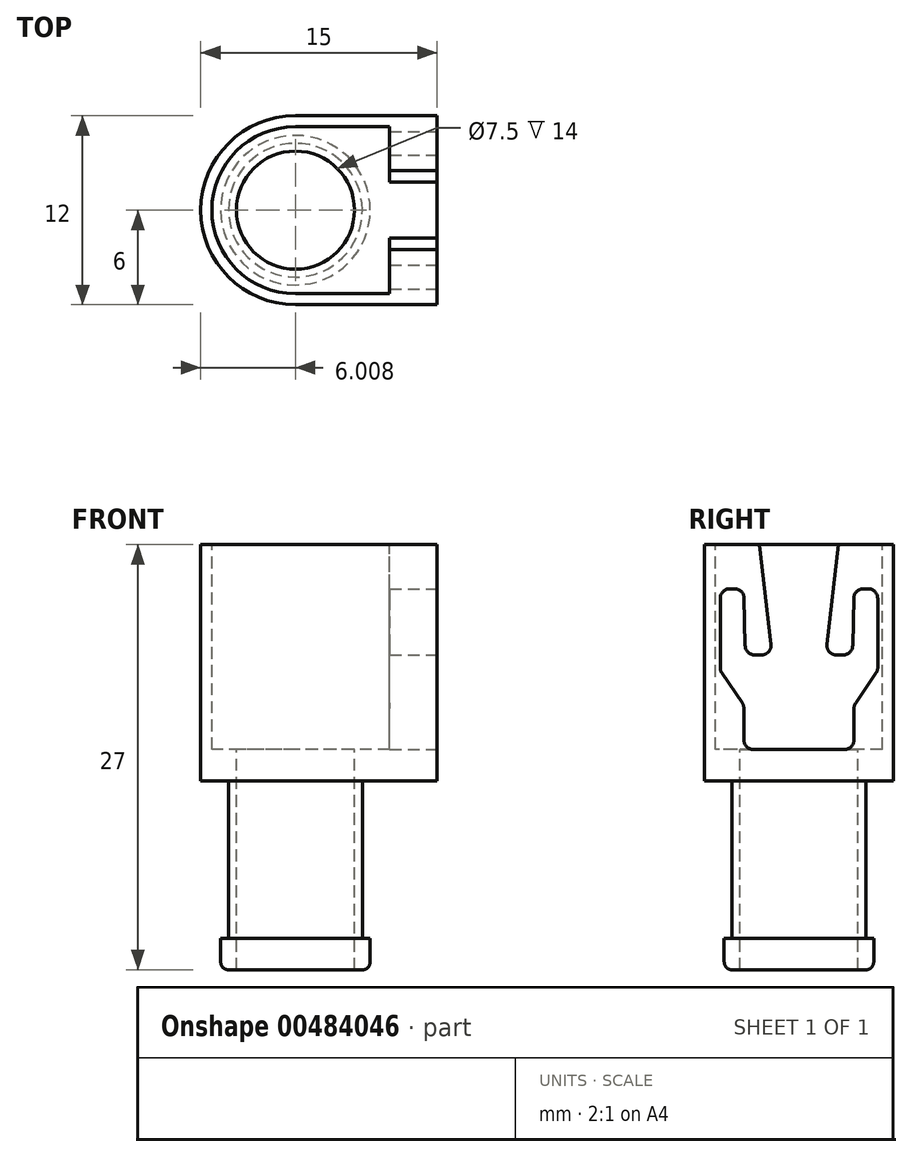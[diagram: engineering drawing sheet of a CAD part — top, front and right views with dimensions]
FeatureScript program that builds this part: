
annotation { "Feature Type Name" : "Feature", "Feature Type Description" : "" }
export const myFeature = defineFeature(function(context is Context, id is Id, definition is map)
    precondition{}
    {
        {
            var Q0;
            Q0=qCreatedBy(makeId("Top.planeOp"),FACE);
            var sketch = newSketch(context, id + "F0", { "sketchPlane" : qUnion([Q0])});
            skLineSegment(sketch, "E0", {"start": v(-9, 6) * mm, "end": v(0, 6) * mm});
            skLineSegment(sketch, "E1", {"start": v(0, 6) * mm, "end": v(0, -6) * mm});
            skLineSegment(sketch, "E2", {"start": v(0, -6) * mm, "end": v(-9, -6) * mm});
            skArc(sketch, "E3", {"start": v(-9, 6) * mm, "mid": v(-15, 0) * mm, "end": v(-9, -6) * mm});
            skSolve(sketch);
        }
        {
            var Q0;
            Q0=makeQuery(id+"F0.imprint","IMPRINT",FACE,{"disambiguationData":[TD([[makeQuery(id+"F0.imprint","IMPRINT",EDGE,{"derivedFrom":sQuery(id+"F0.wireOp",EDGE,"E0")}),-1.0]])]});
            extrude(context, id + "F1", {"entities" : qUnion([Q0]), "depth" : 15 * mm});
        }
        {
            var Q0;
            Q0=qCreatedBy(makeId("Top.planeOp"),FACE);
            var sketch = newSketch(context, id + "F2", { "sketchPlane" : qUnion([Q0])});
            skCircle(sketch, "E4", {"center": v(-9, 0) * mm, "radius": 4.25 * mm});
            skCircle(sketch, "E5", {"center": v(-9, 0) * mm, "radius": 3.75 * mm});
            skSolve(sketch);
        }
        {
            var Q0;
            Q0=makeQuery(id+"F2.imprint","IMPRINT",FACE,{"disambiguationData":[TD([[makeQuery(id+"F2.imprint","IMPRINT",EDGE,{"derivedFrom":sQuery(id+"F2.wireOp",EDGE,"E4")}),1.0]])]});
            extrude(context, id + "F3", {"entities" : qUnion([Q0]), "operationType" : NewBodyOperationType.ADD, "oppositeDirection" : true, "depth" : 10 * mm});
        }
        {
            var Q0;
            Q0=makeQuery(id+"F3.opExtrude","CAP_FACE",FACE,{"disambiguationData":[OSD([sQuery(id+"F2.wireOp",EDGE,"E4"),sQuery(id+"F2.wireOp",EDGE,"E5")])],"isStart":false});
            var sketch = newSketch(context, id + "F4", { "sketchPlane" : qUnion([Q0])});
            skCircle(sketch, "E6", {"center": v(-9, 0) * mm, "radius": 4.75 * mm});
            skSolve(sketch);
        }
        {
            var Q0;
            Q0=makeQuery(id+"F4.imprint","IMPRINT",FACE,{"disambiguationData":[TD([[makeQuery(id+"F4.imprint","IMPRINT",EDGE,{"derivedFrom":makeQuery(id+"F3.opExtrude","CAP_EDGE",EDGE,{"disambiguationData":[OSD([sQuery(id+"F2.wireOp",EDGE,"E4")])],"isStart":false})}),-1.0]])]});
            var Q1;
            Q1=makeQuery(id+"F4.imprint","IMPRINT",FACE,{"disambiguationData":[TD([[makeQuery(id+"F4.imprint","IMPRINT",EDGE,{"derivedFrom":sQuery(id+"F4.wireOp",EDGE,"E6")}),1.0]])]});
            extrude(context, id + "F5", {"entities" : qUnion([Q0, Q1]), "operationType" : NewBodyOperationType.ADD, "depth" : 2 * mm});
        }
        {
            var Q0;
            Q0=makeQuery(id+"F1.opExtrude","CAP_FACE",FACE,{"disambiguationData":[OSD([sQuery(id+"F0.wireOp",EDGE,"E0"),sQuery(id+"F0.wireOp",EDGE,"E1"),sQuery(id+"F0.wireOp",EDGE,"E2"),sQuery(id+"F0.wireOp",EDGE,"E3")])],"isStart":false});
            var sketch = newSketch(context, id + "F6", { "sketchPlane" : qUnion([Q0])});
            skLineSegment(sketch, "E7", {"start": v(-3, 5.3) * mm, "end": v(-9, 5.3) * mm});
            skLineSegment(sketch, "E8", {"start": v(-3, 5.3) * mm, "end": v(-3, -5.3) * mm});
            skLineSegment(sketch, "E9", {"start": v(-3, -5.3) * mm, "end": v(-9, -5.3) * mm});
            skArc(sketch, "E10", {"start": v(-9, 5.3) * mm, "mid": v(-14.3, 0) * mm, "end": v(-9, -5.3) * mm});
            skSolve(sketch);
        }
        {
            var Q0;
            Q0=makeQuery(id+"F6.imprint","IMPRINT",FACE,{"disambiguationData":[TD([[makeQuery(id+"F6.imprint","IMPRINT",EDGE,{"derivedFrom":sQuery(id+"F6.wireOp",EDGE,"E7")}),1.0]])]});
            var Q1;
            {var subQ0=sQuery(id+"F0.wireOp",EDGE,"E2");var subQ1=sQuery(id+"F0.wireOp",EDGE,"E1");var subQ2=sQuery(id+"F0.wireOp",EDGE,"E3");var subQ3=sQuery(id+"F0.wireOp",EDGE,"E0");Q1=makeQuery(id+"F3.boolean.opBoolean","SPLIT",FACE,{"disambiguationData":[TD([makeQuery(id+"F1.opExtrude","SWEPT_FACE",FACE,{"disambiguationData":[OSD([subQ3])]})])],"derivedFrom":makeQuery(id+"F1.opExtrude","CAP_FACE",FACE,{"disambiguationData":[OSD([subQ3,subQ1,subQ0,subQ2])],"isStart":true})});}
            extrude(context, id + "F7", {"entities" : qUnion([Q0]), "operationType" : NewBodyOperationType.REMOVE, "oppositeDirection" : true, "endBoundEntityFace" : qUnion([Q1]), "depth" : 13 * mm, "offsetDistance" : 25.4 * mm});
        }
        {
            var Q0;
            Q0=makeQuery(id+"F3.boolean.opBoolean","SPLIT",FACE,{"disambiguationData":[TD([makeQuery(id+"F3.opExtrude","SWEPT_FACE",FACE,{"disambiguationData":[OSD([sQuery(id+"F2.wireOp",EDGE,"E5")])]})])],"derivedFrom":makeQuery(id+"F1.opExtrude","CAP_FACE",FACE,{"disambiguationData":[OSD([sQuery(id+"F0.wireOp",EDGE,"E0"),sQuery(id+"F0.wireOp",EDGE,"E1"),sQuery(id+"F0.wireOp",EDGE,"E2"),sQuery(id+"F0.wireOp",EDGE,"E3")])],"isStart":true})});
            var Q1;
            Q1=makeQuery(id+"F7.boolean.opBoolean","COPY",FACE,{"derivedFrom":makeQuery(id+"F7.opExtrude","CAP_FACE",FACE,{"disambiguationData":[OSD([sQuery(id+"F6.wireOp",EDGE,"E7"),sQuery(id+"F6.wireOp",EDGE,"E8"),sQuery(id+"F6.wireOp",EDGE,"E9"),sQuery(id+"F6.wireOp",EDGE,"E10")])],"isStart":false})});
            extrude(context, id + "F8", {"entities" : qUnion([Q0]), "operationType" : NewBodyOperationType.REMOVE, "endBound" : BoundingType.UP_TO_SURFACE, "oppositeDirection" : true, "endBoundEntityFace" : qUnion([Q1]), "depth" : 25.4 * mm, "offsetDistance" : 25.4 * mm});
        }
        {
            var Q0;
            Q0=makeQuery(id+"F1.opExtrude","SWEPT_FACE",FACE,{"disambiguationData":[OSD([sQuery(id+"F0.wireOp",EDGE,"E1")])]});
            var sketch = newSketch(context, id + "F9", { "sketchPlane" : qUnion([Q0])});
            skLineSegment(sketch, "E11", {"start": v(-3.5, 2.6) * mm, "end": v(-3.5, 4.61) * mm});
            skLineSegment(sketch, "E12", {"start": v(-3.6, 4.95) * mm, "end": v(-4.9, 6.85) * mm});
            skLineSegment(sketch, "E13", {"start": v(-5, 7.19) * mm, "end": v(-5, 11.6) * mm});
            skLineSegment(sketch, "E14", {"start": v(-4.4, 12.2) * mm, "end": v(-4.1, 12.2) * mm});
            skLineSegment(sketch, "E15", {"start": v(-3.49, 11.6) * mm, "end": v(-3.41, 8.6) * mm});
            skLineSegment(sketch, "E16", {"start": v(-2.8, 8) * mm, "end": v(-2.38, 8) * mm});
            skLineSegment(sketch, "E17", {"start": v(-1.78, 8.67) * mm, "end": v(-2.5, 14.97) * mm});
            skLineSegment(sketch, "E18", {"start": v(-2.9, 2) * mm, "end": v(0, 2) * mm});
            skLineSegment(sketch, "E19.MirrorCS", {"start": v(1.78, 8.67) * mm, "end": v(2.5, 14.97) * mm});
            skLineSegment(sketch, "E20.MirrorCS", {"start": v(2.8, 8) * mm, "end": v(2.38, 8) * mm});
            skLineSegment(sketch, "E21.MirrorCS", {"start": v(3.49, 11.6) * mm, "end": v(3.41, 8.6) * mm});
            skLineSegment(sketch, "E22.MirrorCS", {"start": v(4.4, 12.2) * mm, "end": v(4.1, 12.2) * mm});
            skLineSegment(sketch, "E23.MirrorCS", {"start": v(5, 7.19) * mm, "end": v(5, 11.6) * mm});
            skLineSegment(sketch, "E24.MirrorCS", {"start": v(3.6, 4.95) * mm, "end": v(4.9, 6.85) * mm});
            skLineSegment(sketch, "E25.MirrorCS", {"start": v(2.9, 2) * mm, "end": v(0, 2) * mm});
            skLineSegment(sketch, "E26.MirrorCS", {"start": v(3.5, 2.6) * mm, "end": v(3.5, 4.61) * mm});
            skPoint(sketch, "E27.visualSharp", {"position": v(3.4, 8) * mm});
            skArc(sketch, "E27.filletArc", {"start": v(2.8, 8) * mm, "mid": v(3.23, 8.17) * mm, "end": v(3.41, 8.6) * mm});
            skPoint(sketch, "E28.visualSharp", {"position": v(1.7, 8) * mm});
            skArc(sketch, "E28.filletArc", {"start": v(1.78, 8.67) * mm, "mid": v(1.93, 8.2) * mm, "end": v(2.38, 8) * mm});
            skPoint(sketch, "E29.visualSharp", {"position": v(-1.7, 8) * mm});
            skArc(sketch, "E29.filletArc", {"start": v(-2.38, 8) * mm, "mid": v(-1.93, 8.2) * mm, "end": v(-1.78, 8.67) * mm});
            skPoint(sketch, "E30.visualSharp", {"position": v(-3.4, 8) * mm});
            skArc(sketch, "E30.filletArc", {"start": v(-3.41, 8.6) * mm, "mid": v(-3.23, 8.17) * mm, "end": v(-2.8, 8) * mm});
            skPoint(sketch, "E31.visualSharp", {"position": v(-3.5, 12.2) * mm});
            skArc(sketch, "E31.filletArc", {"start": v(-3.49, 11.6) * mm, "mid": v(-3.67, 12.03) * mm, "end": v(-4.1, 12.2) * mm});
            skPoint(sketch, "E32.visualSharp", {"position": v(3.5, 12.2) * mm});
            skArc(sketch, "E32.filletArc", {"start": v(4.1, 12.2) * mm, "mid": v(3.67, 12.03) * mm, "end": v(3.49, 11.6) * mm});
            skPoint(sketch, "E33.visualSharp", {"position": v(5, 12.2) * mm});
            skArc(sketch, "E33.filletArc", {"start": v(5, 11.6) * mm, "mid": v(4.82, 12.02) * mm, "end": v(4.4, 12.2) * mm});
            skPoint(sketch, "E34.visualSharp", {"position": v(-5, 12.2) * mm});
            skArc(sketch, "E34.filletArc", {"start": v(-4.4, 12.2) * mm, "mid": v(-4.82, 12.02) * mm, "end": v(-5, 11.6) * mm});
            skPoint(sketch, "E35.visualSharp", {"position": v(-5, 7) * mm});
            skArc(sketch, "E35.filletArc", {"start": v(-5, 7.19) * mm, "mid": v(-4.97, 7) * mm, "end": v(-4.9, 6.85) * mm});
            skPoint(sketch, "E36.visualSharp", {"position": v(5, 7) * mm});
            skArc(sketch, "E36.filletArc", {"start": v(4.9, 6.85) * mm, "mid": v(4.97, 7) * mm, "end": v(5, 7.19) * mm});
            skPoint(sketch, "E37.visualSharp", {"position": v(3.5, 4.8) * mm});
            skArc(sketch, "E37.filletArc", {"start": v(3.6, 4.95) * mm, "mid": v(3.53, 4.8) * mm, "end": v(3.5, 4.61) * mm});
            skPoint(sketch, "E38.visualSharp", {"position": v(3.5, 2) * mm});
            skArc(sketch, "E38.filletArc", {"start": v(2.9, 2) * mm, "mid": v(3.32, 2.18) * mm, "end": v(3.5, 2.6) * mm});
            skPoint(sketch, "E39.visualSharp", {"position": v(-3.5, 2) * mm});
            skArc(sketch, "E39.filletArc", {"start": v(-3.5, 2.6) * mm, "mid": v(-3.32, 2.18) * mm, "end": v(-2.9, 2) * mm});
            skPoint(sketch, "E40.visualSharp", {"position": v(-3.5, 4.8) * mm});
            skArc(sketch, "E40.filletArc", {"start": v(-3.5, 4.61) * mm, "mid": v(-3.53, 4.8) * mm, "end": v(-3.6, 4.95) * mm});
            skLineSegment(sketch, "E41", {"start": v(-2.5, 14.97) * mm, "end": v(-2.82, 15.95) * mm});
            skLineSegment(sketch, "E42", {"start": v(2.5, 14.97) * mm, "end": v(2.63, 16.06) * mm});
            skLineSegment(sketch, "E43", {"start": v(2.63, 16.06) * mm, "end": v(-2.82, 15.95) * mm});
            skSolve(sketch);
        }
        {
            var Q0;
            Q0=makeQuery(id+"F9.imprint","IMPRINT",FACE,{"disambiguationData":[TD([[makeQuery(id+"F9.imprint","IMPRINT",EDGE,{"derivedFrom":sQuery(id+"F9.wireOp",EDGE,"E11")}),-1.0]])]});
            var Q1;
            Q1=makeQuery(id+"F7.boolean.opBoolean","COPY",FACE,{"derivedFrom":makeQuery(id+"F7.opExtrude","SWEPT_FACE",FACE,{"disambiguationData":[OSD([sQuery(id+"F6.wireOp",EDGE,"E8")])]})});
            extrude(context, id + "F10", {"entities" : qUnion([Q0, Q1]), "operationType" : NewBodyOperationType.REMOVE, "oppositeDirection" : true, "depth" : 5 * mm, "offsetDistance" : 25.4 * mm});
        }
        {
            var Q0;
            Q0=makeQuery(id+"F5.opExtrude","CAP_EDGE",EDGE,{"disambiguationData":[OSD([sQuery(id+"F4.wireOp",EDGE,"E6")])],"isStart":false});
            fillet(context, id + "F11", {"entities" : qUnion([Q0]), "radius" : 0.5 * mm, "tangentPropagation" : true, "allowEdgeOverflow" : false});
        }
    });
